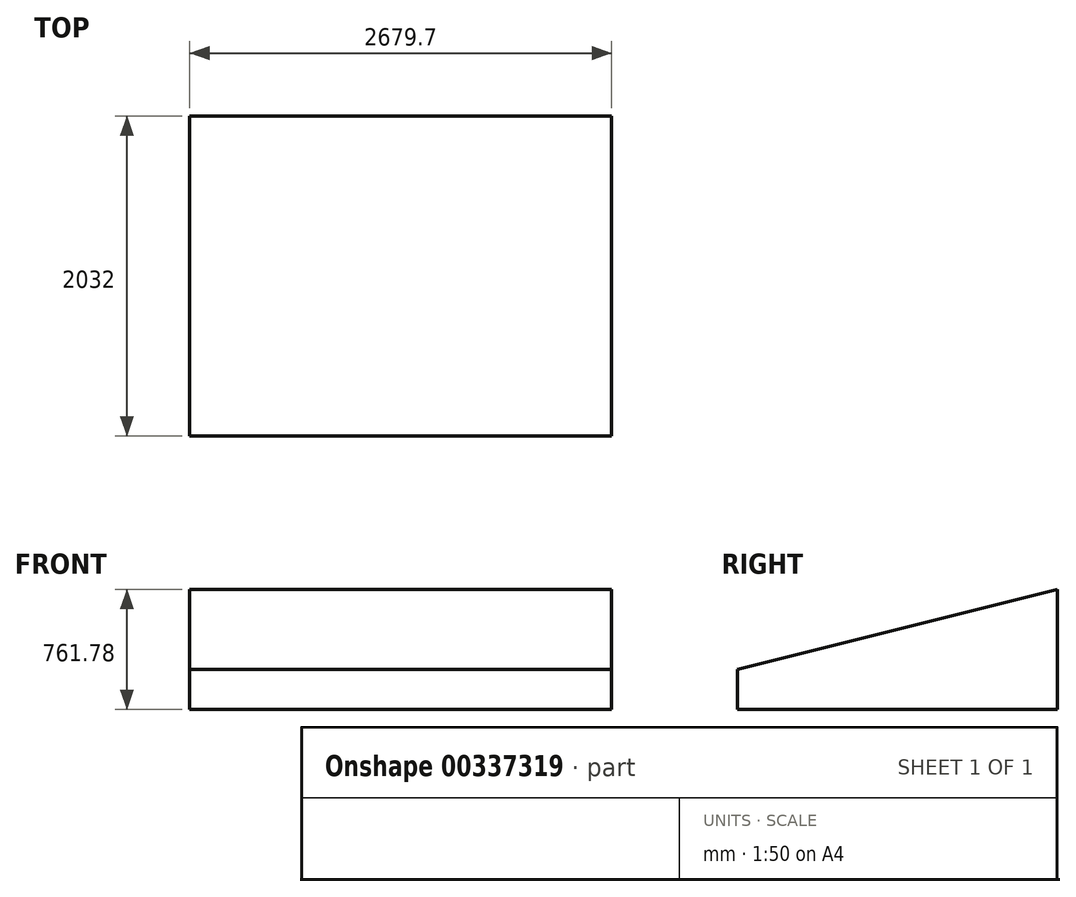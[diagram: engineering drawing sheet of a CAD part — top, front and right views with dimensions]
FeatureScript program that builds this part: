
annotation { "Feature Type Name" : "Feature", "Feature Type Description" : "" }
export const myFeature = defineFeature(function(context is Context, id is Id, definition is map)
    precondition{}
    {
        {
            var Q0;
            Q0=qCreatedBy(makeId("Right.planeOp"),FACE);
            var sketch = newSketch(context, id + "F0", { "sketchPlane" : qUnion([Q0])});
            skLineSegment(sketch, "E0", {"start": v(725.96, 761.78) * mm, "end": v(725.96, 0) * mm});
            skLineSegment(sketch, "E1", {"start": v(725.96, 0) * mm, "end": v(-1306.04, 0) * mm});
            skLineSegment(sketch, "E2", {"start": v(-1306.04, 0) * mm, "end": v(-1306.04, 254) * mm});
            skLineSegment(sketch, "E3", {"start": v(-1306.04, 254) * mm, "end": v(725.96, 761.78) * mm});
            skSolve(sketch);
        }
        {
            var Q0;
            Q0 = qSketchRegion(id + "F0", true);
            extrude(context, id + "F1", {"entities" : qUnion([Q0]), "depth" : 2679.7 * mm});
        }
        {
            var Q0;
            Q0=makeQuery(id+"F1.opExtrude","SWEPT_FACE",FACE,{"disambiguationData":[OSD([sQuery(id+"F0.wireOp",EDGE,"E3")])]});
            var sketch = newSketch(context, id + "F2", { "sketchPlane" : qUnion([Q0])});
            skLineSegment(sketch, "E4.bottom", {"start": v(805.48, -1205.5) * mm, "end": v(1941.38, -1205.5) * mm});
            skLineSegment(sketch, "E4.top", {"start": v(805.48, 420.87) * mm, "end": v(1941.38, 420.87) * mm});
            skLineSegment(sketch, "E4.left", {"start": v(805.48, -1205.5) * mm, "end": v(805.48, 420.87) * mm});
            skLineSegment(sketch, "E4.right", {"start": v(1941.38, -1205.5) * mm, "end": v(1941.38, 420.87) * mm});
            skSolve(sketch);
        }
        {
            var Q0;
            Q0=makeQuery(id+"F2.imprint","IMPRINT",FACE,{"disambiguationData":[TD([[makeQuery(id+"F2.imprint","IMPRINT",EDGE,{"derivedFrom":sQuery(id+"F2.wireOp",EDGE,"E4.bottom")}),-1.0]])]});
            extrude(context, id + "F3", {"entities" : qUnion([Q0]), "operationType" : NewBodyOperationType.ADD, "depth" : -254 * mm});
        }
    });
